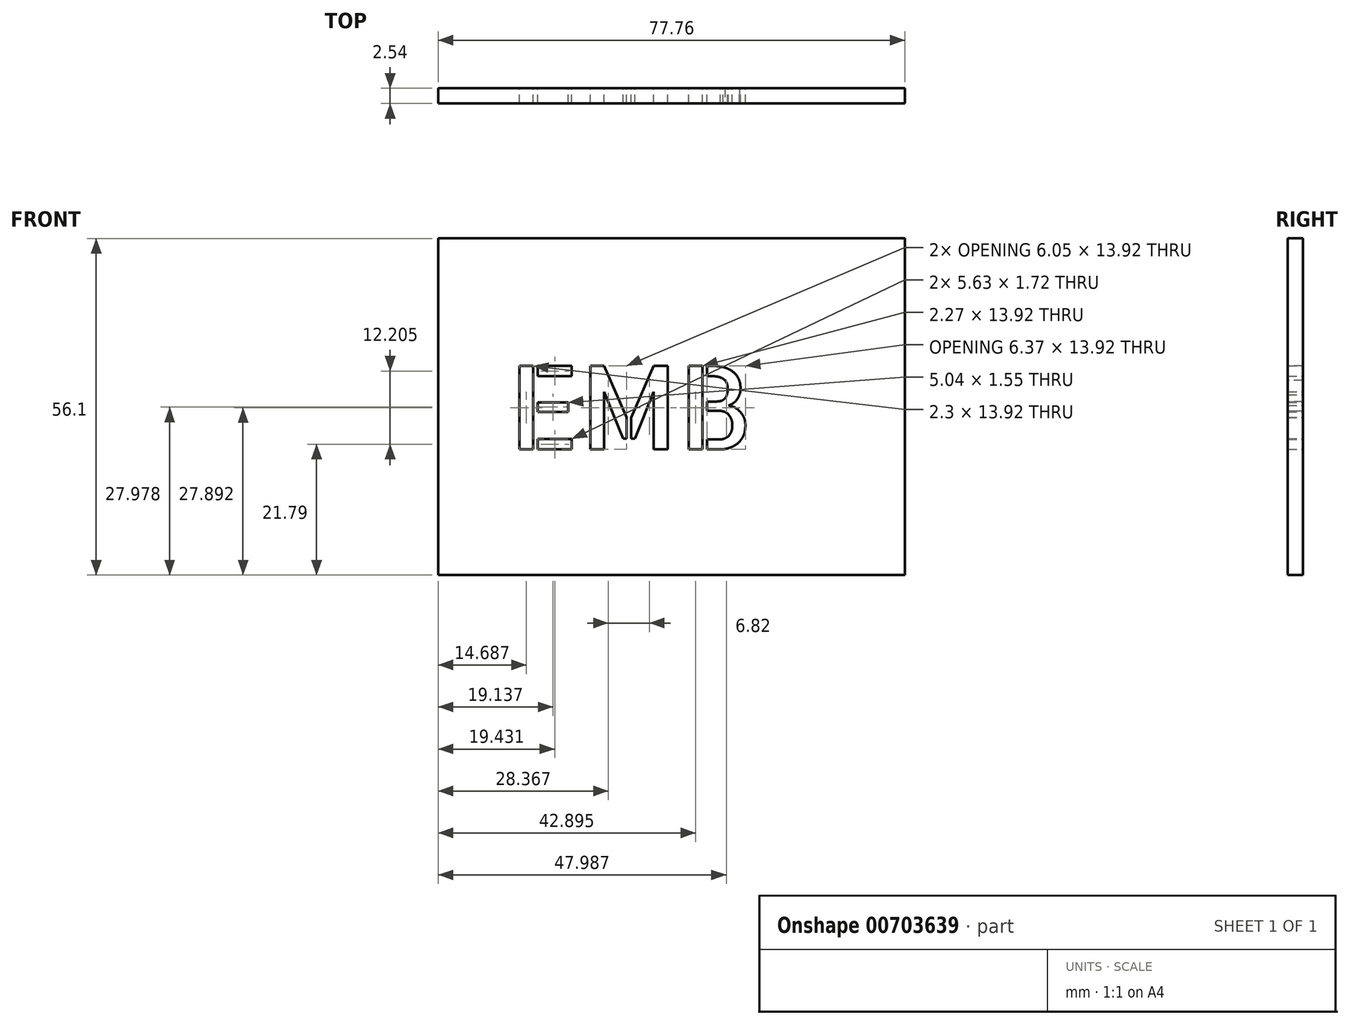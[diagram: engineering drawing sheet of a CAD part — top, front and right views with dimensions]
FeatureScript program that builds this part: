
annotation { "Feature Type Name" : "Feature", "Feature Type Description" : "" }
export const myFeature = defineFeature(function(context is Context, id is Id, definition is map)
    precondition{}
    {
        {
            var Q0;
            Q0=qCreatedBy(makeId("Front.planeOp"),FACE);
            var sketch = newSketch(context, id + "F0", { "sketchPlane" : qUnion([Q0])});
            skText(sketch, "E0", { "text": "EMB", "fontName": "AllertaStencil-Regular.ttf"});
            skLineSegment(sketch, "E1.bottom", {"start": v(-11.74, 35.17) * mm, "end": v(66.02, 35.17) * mm});
            skLineSegment(sketch, "E1.top", {"start": v(-11.74, -20.93) * mm, "end": v(66.02, -20.93) * mm});
            skLineSegment(sketch, "E1.left", {"start": v(-11.74, 35.17) * mm, "end": v(-11.74, -20.93) * mm});
            skLineSegment(sketch, "E1.right", {"start": v(66.02, 35.17) * mm, "end": v(66.02, -20.93) * mm});
            const initialGuessF0  = {"E0": [0, 0, 1, 0, 0.01393]};
            skSetInitialGuess(sketch, initialGuessF0);
            skSolve(sketch);
        }
        {
            var Q0;
            Q0 = qSketchRegion(id + "F0", true);
            extrude(context, id + "F1", {"entities" : qUnion([Q0]), "depth" : 2.54 * mm, "offsetDistance" : 25.4 * mm});
        }
    });
